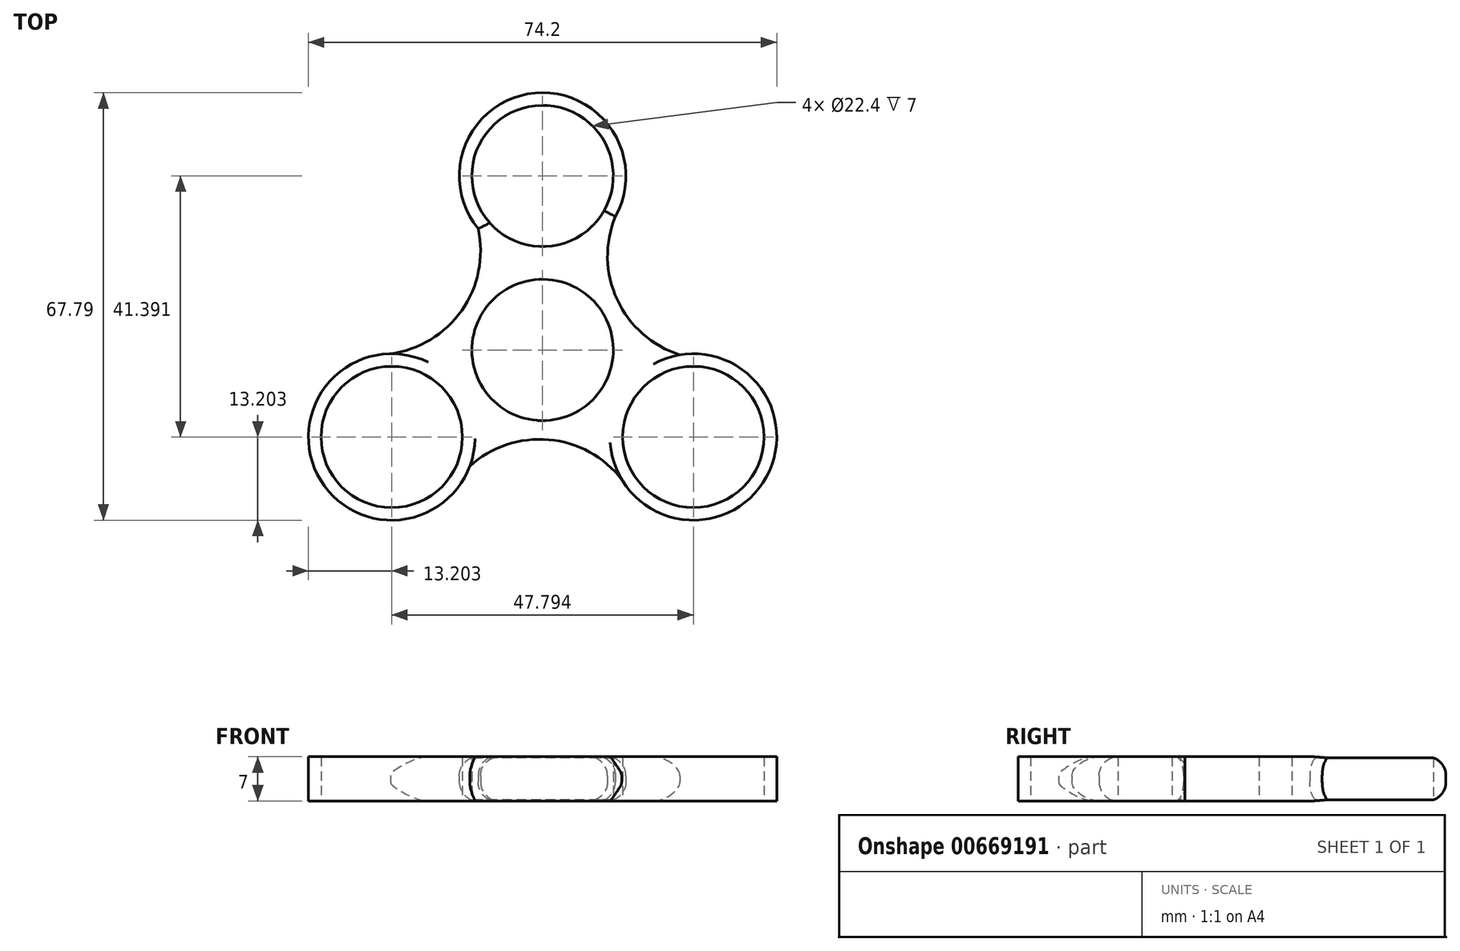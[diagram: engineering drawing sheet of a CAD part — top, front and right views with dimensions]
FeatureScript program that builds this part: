
annotation { "Feature Type Name" : "Feature", "Feature Type Description" : "" }
export const myFeature = defineFeature(function(context is Context, id is Id, definition is map)
    precondition{}
    {
        {
            var Q0;
            Q0=qCreatedBy(makeId("Top.planeOp"),FACE);
            var sketch = newSketch(context, id + "F0", { "sketchPlane" : qUnion([Q0])});
            skCircle(sketch, "E0", {"center": v(0, 0) * mm, "radius": 11.2 * mm});
            skCircle(sketch, "E1", {"center": v(0, 27.6) * mm, "radius": 11.2 * mm});
            skArc(sketch, "E2", {"start": v(11.54, 21.18) * mm, "mid": v(-1.18, 40.74) * mm, "end": v(-10.2, 19.22) * mm});
            skArc(sketch, "E3.1.0", {"start": v(-24.1, -0.6) * mm, "mid": v(-34.7, -21.4) * mm, "end": v(-11.54, -18.45) * mm});
            skCircle(sketch, "E3.1.1", {"center": v(-23.9, -13.8) * mm, "radius": 11.2 * mm});
            skArc(sketch, "E3.2.0", {"start": v(12.57, -20.58) * mm, "mid": v(35.87, -19.35) * mm, "end": v(21.75, -0.77) * mm});
            skCircle(sketch, "E3.2.1", {"center": v(23.9, -13.8) * mm, "radius": 11.2 * mm});
            skArc(sketch, "E4", {"start": v(11.54, 21.18) * mm, "mid": v(11.83, 7.96) * mm, "end": v(21.75, -0.77) * mm});
            skArc(sketch, "E5.1.0", {"start": v(-24.1, -0.6) * mm, "mid": v(-12.81, 6.26) * mm, "end": v(-10.2, 19.22) * mm});
            skArc(sketch, "E5.2.0", {"start": v(12.57, -20.58) * mm, "mid": v(0.98, -14.23) * mm, "end": v(-11.54, -18.45) * mm});
            skSolve(sketch);
        }
        {
            var Q0;
            Q0=makeQuery(id+"F0.imprint","IMPRINT",FACE,{"disambiguationData":[TD([[makeQuery(id+"F0.imprint","IMPRINT",EDGE,{"derivedFrom":sQuery(id+"F0.wireOp",EDGE,"E0")}),-1.0]])]});
            extrude(context, id + "F1", {"entities" : qUnion([Q0]), "depth" : 7 * mm, "offsetDistance" : 25 * mm});
        }
        {
            var Q0;
            Q0=makeQuery(id+"F1.opExtrude","CAP_EDGE",EDGE,{"disambiguationData":[OSD([sQuery(id+"F0.wireOp",EDGE,"E5.2.0")])],"isStart":false});
            var Q1;
            Q1=makeQuery(id+"F1.opExtrude","CAP_EDGE",EDGE,{"disambiguationData":[OSD([sQuery(id+"F0.wireOp",EDGE,"E3.2.0")])],"isStart":false});
            var Q2;
            Q2=makeQuery(id+"F1.opExtrude","CAP_EDGE",EDGE,{"disambiguationData":[OSD([sQuery(id+"F0.wireOp",EDGE,"E4")])],"isStart":false});
            var Q3;
            Q3=makeQuery(id+"F1.opExtrude","CAP_EDGE",EDGE,{"disambiguationData":[OSD([sQuery(id+"F0.wireOp",EDGE,"E2")])],"isStart":false});
            var Q4;
            Q4=makeQuery(id+"F1.opExtrude","CAP_EDGE",EDGE,{"disambiguationData":[OSD([sQuery(id+"F0.wireOp",EDGE,"E5.1.0")])],"isStart":false});
            var Q5;
            Q5=makeQuery(id+"F1.opExtrude","CAP_EDGE",EDGE,{"disambiguationData":[OSD([sQuery(id+"F0.wireOp",EDGE,"E3.1.0")])],"isStart":false});
            var Q6;
            Q6=makeQuery(id+"F1.opExtrude","CAP_EDGE",EDGE,{"disambiguationData":[OSD([sQuery(id+"F0.wireOp",EDGE,"E3.1.0")])],"isStart":true});
            var Q7;
            Q7=makeQuery(id+"F1.opExtrude","CAP_EDGE",EDGE,{"disambiguationData":[OSD([sQuery(id+"F0.wireOp",EDGE,"E5.1.0")])],"isStart":true});
            var Q8;
            Q8=makeQuery(id+"F1.opExtrude","CAP_EDGE",EDGE,{"disambiguationData":[OSD([sQuery(id+"F0.wireOp",EDGE,"E2")])],"isStart":true});
            var Q9;
            Q9=makeQuery(id+"F1.opExtrude","CAP_EDGE",EDGE,{"disambiguationData":[OSD([sQuery(id+"F0.wireOp",EDGE,"E4")])],"isStart":true});
            var Q10;
            Q10=makeQuery(id+"F1.opExtrude","CAP_EDGE",EDGE,{"disambiguationData":[OSD([sQuery(id+"F0.wireOp",EDGE,"E3.2.0")])],"isStart":true});
            var Q11;
            Q11=makeQuery(id+"F1.opExtrude","CAP_EDGE",EDGE,{"disambiguationData":[OSD([sQuery(id+"F0.wireOp",EDGE,"E5.2.0")])],"isStart":true});
            fillet(context, id + "F2", {"entities" : qUnion([Q0, Q1, Q2, Q3, Q4, Q5, Q6, Q7, Q8, Q9, Q10, Q11]), "radius" : 3 * mm, "tangentPropagation" : true, "allowEdgeOverflow" : false});
        }
    });
